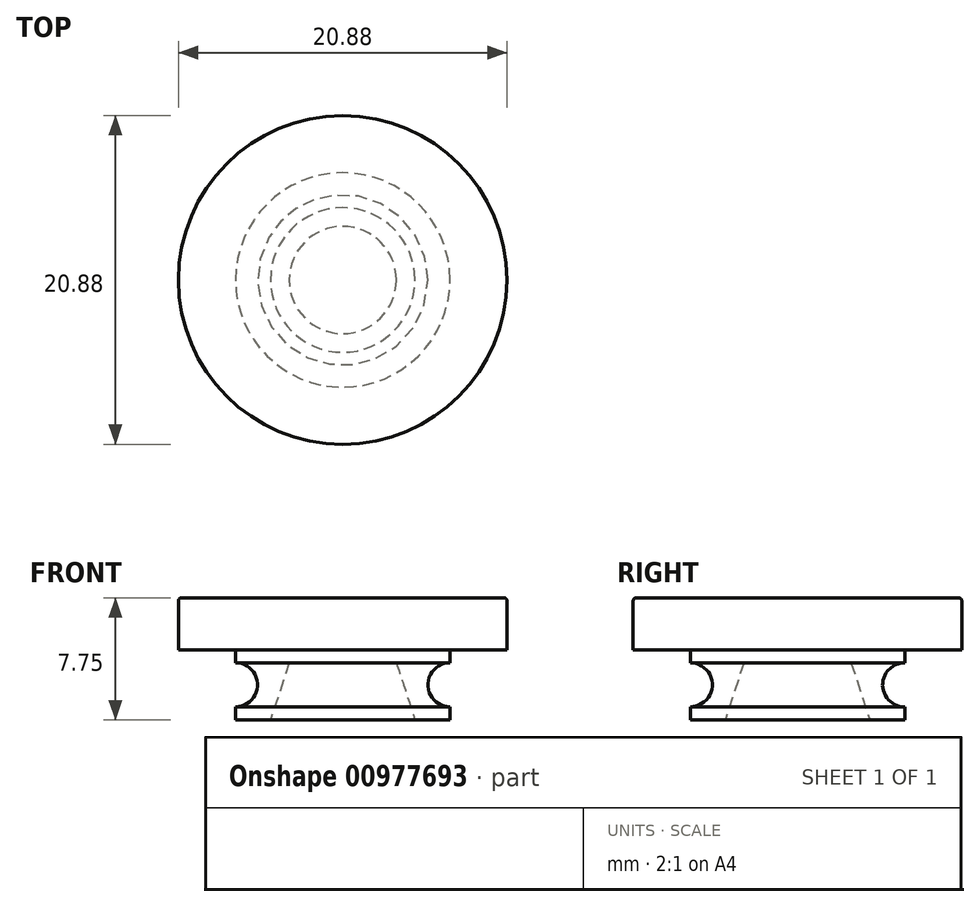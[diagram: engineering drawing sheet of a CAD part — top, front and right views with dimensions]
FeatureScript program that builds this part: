
annotation { "Feature Type Name" : "Feature", "Feature Type Description" : "" }
export const myFeature = defineFeature(function(context is Context, id is Id, definition is map)
    precondition{}
    {
        {
            var Q0;
            Q0=qCreatedBy(makeId("Front.planeOp"),FACE);
            var sketch = newSketch(context, id + "F0", { "sketchPlane" : qUnion([Q0])});
            skLineSegment(sketch, "E0", {"start": v(0, 55.9) * mm, "end": v(0, -42.19) * mm, "construction": true});
            skLineSegment(sketch, "E1", {"start": v(0, 14.42) * mm, "end": v(10.44, 14.42) * mm});
            skLineSegment(sketch, "E2", {"start": v(10.44, 14.42) * mm, "end": v(10.44, 11.12) * mm});
            skLineSegment(sketch, "E3", {"start": v(10.44, 11.12) * mm, "end": v(6.81, 11.12) * mm});
            skLineSegment(sketch, "E4", {"start": v(6.81, 11.12) * mm, "end": v(6.81, 10.3) * mm});
            skLineSegment(sketch, "E5", {"start": v(6.81, 6.67) * mm, "end": v(4.59, 6.67) * mm});
            skArc(sketch, "E6", {"start": v(6.8, 10.3) * mm, "mid": v(5.41, 8.9) * mm, "end": v(6.81, 7.5) * mm});
            skLineSegment(sketch, "E7.trimOffspring", {"start": v(6.81, 7.5) * mm, "end": v(6.81, 6.67) * mm});
            skLineSegment(sketch, "E8", {"start": v(0, 14.42) * mm, "end": v(0, 6.67) * mm});
            skLineSegment(sketch, "E9", {"start": v(4.59, 6.67) * mm, "end": v(3.4, 10.3) * mm});
            skPoint(sketch, "E9.endSnap0", {"position": v(3.4, 6.67) * mm});
            skLineSegment(sketch, "E10", {"start": v(3.4, 10.3) * mm, "end": v(0, 10.3) * mm});
            skSolve(sketch);
        }
        {
            var Q0;
            Q0=makeQuery(id+"F0.imprint","IMPRINT",FACE,{"disambiguationData":[TD([[makeQuery(id+"F0.imprint","IMPRINT",EDGE,{"derivedFrom":sQuery(id+"F0.wireOp",EDGE,"E1")}),-1.0]])]});
            var Q1;
            Q1=sQuery(id+"F0.wireOp",EDGE,"E0");
            revolve(context, id + "F1", {"surfaceOperationType" : NewSurfaceOperationType.NEW, "entities" : qUnion([Q0]), "axis" : qUnion([Q1]), "revolveType" : RevolveType.FULL});
        }
        {
            var Q0;
            Q0=makeQuery(id+"F1.opRevolve","SWEPT_EDGE",EDGE,{"disambiguationData":[OSD([sQuery(id+"F0.wireOp",EDGE,"E1"),sQuery(id+"F0.wireOp",EDGE,"E2")])]});
            fillet(context, id + "F2", {"entities" : qUnion([Q0]), "radius" : .2 * mm, "tangentPropagation" : true, "allowEdgeOverflow" : false});
        }
    });
